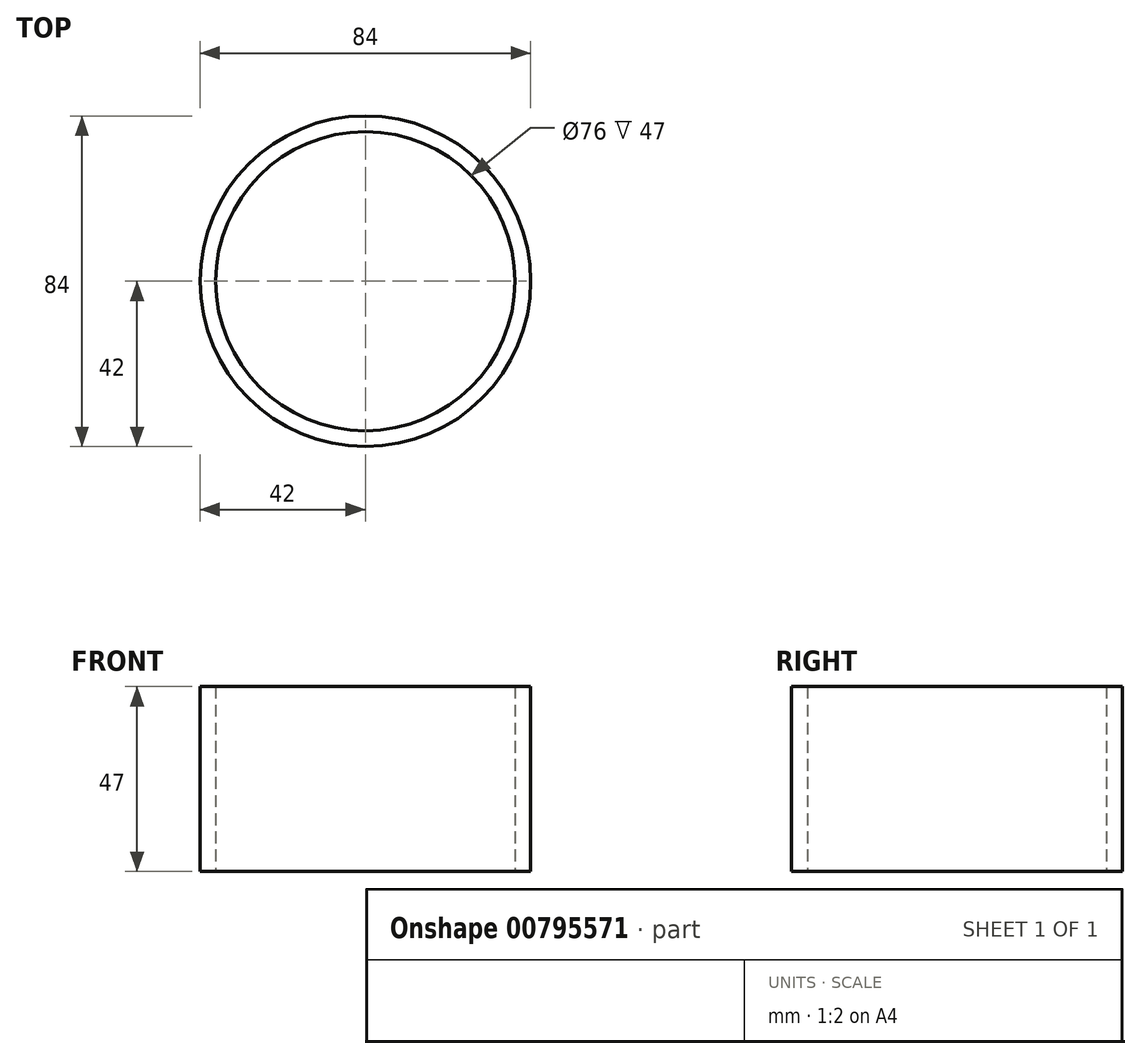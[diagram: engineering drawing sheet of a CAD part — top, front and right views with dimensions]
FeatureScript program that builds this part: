
annotation { "Feature Type Name" : "Feature", "Feature Type Description" : "" }
export const myFeature = defineFeature(function(context is Context, id is Id, definition is map)
    precondition{}
    {
        {
            var Q0;
            Q0=qCreatedBy(makeId("Top.planeOp"),FACE);
            var sketch = newSketch(context, id + "F0", { "sketchPlane" : qUnion([Q0])});
            skCircle(sketch, "E0", {"center": v(0, 0) * mm, "radius": 38 * mm});
            skCircle(sketch, "E1", {"center": v(0, 0) * mm, "radius": 42 * mm});
            skSolve(sketch);
        }
        {
            var Q0;
            Q0=makeQuery(id+"F0.imprint","IMPRINT",FACE,{"disambiguationData":[TD([[makeQuery(id+"F0.imprint","IMPRINT",EDGE,{"derivedFrom":sQuery(id+"F0.wireOp",EDGE,"E0")}),-1.0]])]});
            extrude(context, id + "F1", {"entities" : qUnion([Q0]), "depth" : 47 * mm, "offsetDistance" : 25 * mm});
        }
    });
